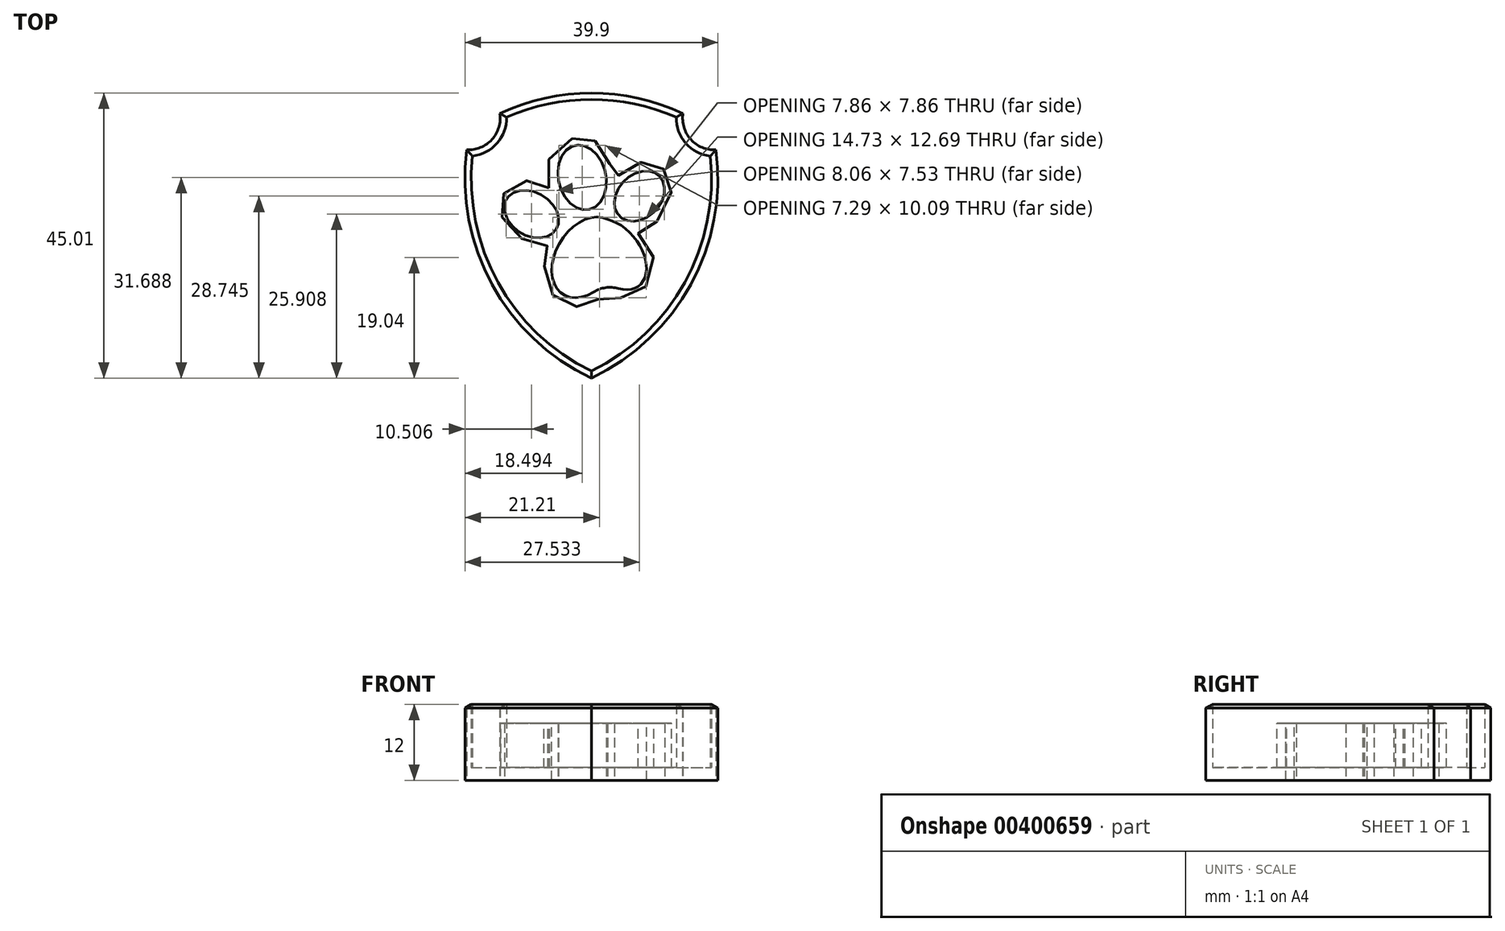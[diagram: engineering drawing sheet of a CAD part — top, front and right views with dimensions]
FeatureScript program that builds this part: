
annotation { "Feature Type Name" : "Feature", "Feature Type Description" : "" }
export const myFeature = defineFeature(function(context is Context, id is Id, definition is map)
    precondition{}
    {
        {
            var Q0;
            Q0=qCreatedBy(makeId("Top.planeOp"),FACE);
            var sketch = newSketch(context, id + "F0", { "sketchPlane" : qUnion([Q0])});
            skLineSegment(sketch, "E0", {"start": v(0, 25) * mm, "end": v(0, -25) * mm, "construction": true});
            skArc(sketch, "E1", {"start": v(-14.44, 19.95) * mm, "mid": v(0, 23.16) * mm, "end": v(14.44, 19.95) * mm});
            skArc(sketch, "E2", {"start": v(-14.44, 19.95) * mm, "mid": v(-15.68, 15.84) * mm, "end": v(-19.65, 14.2) * mm});
            skArc(sketch, "E3", {"start": v(14.44, 19.95) * mm, "mid": v(15.68, 15.84) * mm, "end": v(19.65, 14.2) * mm});
            skArc(sketch, "E4", {"start": v(0, -21.85) * mm, "mid": v(-15.7, -7.03) * mm, "end": v(-19.65, 14.2) * mm});
            skArc(sketch, "E5", {"start": v(19.65, 14.2) * mm, "mid": v(15.7, -7.03) * mm, "end": v(0, -21.85) * mm});
            skSolve(sketch);
        }
        {
            var Q0;
            Q0=qSketchRegion(id+"F0",true);
            extrude(context, id + "F1", {"entities" : qUnion([Q0]), "depth" : 2 * mm});
        }
        {
            var Q0;
            Q0=qCreatedBy(makeId("Top.planeOp"),FACE);
            var sketch = newSketch(context, id + "F2", { "sketchPlane" : qUnion([Q0])});
            skArc(sketch, "E6.0", {"start": v(-14.44, 19.95) * mm, "mid": v(0, 23.16) * mm, "end": v(14.44, 19.95) * mm});
            skArc(sketch, "E6.1", {"start": v(-14.44, 19.95) * mm, "mid": v(-15.68, 15.84) * mm, "end": v(-19.65, 14.2) * mm});
            skArc(sketch, "E6.2", {"start": v(0, -21.85) * mm, "mid": v(-15.7, -7.03) * mm, "end": v(-19.65, 14.2) * mm});
            skArc(sketch, "E6.3", {"start": v(14.44, 19.95) * mm, "mid": v(15.68, 15.84) * mm, "end": v(19.65, 14.2) * mm});
            skArc(sketch, "E7.0", {"start": v(-13.39, 19.33) * mm, "mid": v(-14.89, 15.23) * mm, "end": v(-18.76, 13.22) * mm});
            skArc(sketch, "E7.1", {"start": v(0, -20.74) * mm, "mid": v(-14.73, -6.71) * mm, "end": v(-18.76, 13.22) * mm});
            skArc(sketch, "E7.2", {"start": v(-13.39, 19.33) * mm, "mid": v(0, 22.16) * mm, "end": v(13.39, 19.33) * mm});
            skArc(sketch, "E7.3", {"start": v(13.39, 19.33) * mm, "mid": v(14.89, 15.23) * mm, "end": v(18.76, 13.22) * mm});
            skArc(sketch, "E7.4", {"start": v(18.76, 13.22) * mm, "mid": v(14.73, -6.71) * mm, "end": v(0, -20.74) * mm});
            skArc(sketch, "E8.0", {"start": v(19.65, 14.2) * mm, "mid": v(15.7, -7.03) * mm, "end": v(0, -21.85) * mm});
            skSolve(sketch);
        }
        {
            var Q0;
            Q0=qSketchRegion(id+"F2",true);
            extrude(context, id + "F3", {"entities" : qUnion([Q0]), "operationType" : NewBodyOperationType.ADD, "depth" : 12 * mm});
        }
        {
            var Q0;
            Q0=qCreatedBy(makeId("Top.planeOp"),FACE);
            var sketch = newSketch(context, id + "F4", { "sketchPlane" : qUnion([Q0])});
            skEllipse(sketch, "E9", {"center": v(-9.44, 4.06) * mm, "majorRadius": 4.58 * mm, "minorRadius": 3.42 * mm, "majorAxis": v(0.85, -0.53)});
            skEllipse(sketch, "E10", {"center": v(-1.46, 9.84) * mm, "majorRadius": 5.18 * mm, "minorRadius": 3.74 * mm, "majorAxis": v(0.22, -0.97)});
            skEllipse(sketch, "E11", {"center": v(7.58, 6.9) * mm, "majorRadius": 4.46 * mm, "minorRadius": 3.4 * mm, "majorAxis": v(0.7, 0.7)});
            skEllipticalArc(sketch, "E12", {});
            skEllipticalArc(sketch, "E13", {});
            skPoint(sketch, "E14.visualSharp", {"position": v(2.19, -6.69) * mm});
            skArc(sketch, "E14.filletArc", {"start": v(4.29, -7.69) * mm, "mid": v(2.25, -7.56) * mm, "end": v(0.34, -8.26) * mm});
            const initialGuessF4  = {"E12": [-0.000825658324174583, -0.0027743864338845015, 0.5189781024771581, 0.8547875345073818, 0.006885848797741289, 0.004767301582334577, 0.046636328894096385, 4.077954499657045], "E13": [0.0034836893901228905, -0.0022488562390208244, 0.6385724586285335, -0.7695617032318526, 0.006419216435122319, 0.004185572444733501, 5.533444123706438, 2.4160858860053582]};
            skSetInitialGuess(sketch, initialGuessF4);
            skSolve(sketch);
        }
        {
            var Q0;
            Q0=qCreatedBy(makeId("Top.planeOp"),FACE);
            var sketch = newSketch(context, id + "F5", { "sketchPlane" : qUnion([Q0])});
            skFitSpline(sketch, "E15", {"points": [v(-6.71, 8.16) * mm, v(-9.02, 9.2) * mm, v(-13.12, 8.16) * mm, v(-14.28, 5.63) * mm, v(-13.33, 2.06) * mm, v(-9.02, -0.57) * mm, v(-6.71, -1.2) * mm, v(-7.34, -3.83) * mm, v(-6.3, -8.45) * mm, v(-2.82, -10.55) * mm, v(-0.09, -9.92) * mm, v(2.43, -9.08) * mm, v(5.7, -9.08) * mm, v(9.26, -6.35) * mm, v(9.26, -1.4) * mm, v(7.37, 1.32) * mm, v(10.32, 2.9) * mm, v(12.63, 7.95) * mm, v(11.58, 11) * mm, v(8.84, 12.15) * mm, v(5.59, 11.52) * mm, v(3.48, 9.63) * mm, v(2.43, 13.73) * mm, v(0.02, 15.83) * mm, v(-2.82, 16.04) * mm, v(-6.71, 12.57) * mm, v(-6.71, 8.16) * mm]});
            skSolve(sketch);
        }
        {
            var Q0;
            Q0=qSketchRegion(id+"F5",true);
            extrude(context, id + "F6", {"entities" : qUnion([Q0]), "operationType" : NewBodyOperationType.ADD, "depth" : 9 * mm});
        }
        {
            var Q0;
            Q0=qSketchRegion(id+"F4",true);
            extrude(context, id + "F7", {"entities" : qUnion([Q0]), "operationType" : NewBodyOperationType.REMOVE, "endBound" : BoundingType.THROUGH_ALL, "depth" : 25 * mm});
        }
        {
            var Q0;
            Q0=makeQuery(id+"F3.opExtrude","CAP_EDGE",EDGE,{"disambiguationData":[OSD([sQuery(id+"F2.wireOp",EDGE,"E6.2")])],"isStart":false});
            var Q1;
            Q1=makeQuery(id+"F3.opExtrude","CAP_EDGE",EDGE,{"disambiguationData":[OSD([sQuery(id+"F2.wireOp",EDGE,"E6.1")])],"isStart":false});
            var Q2;
            Q2=makeQuery(id+"F3.opExtrude","CAP_EDGE",EDGE,{"disambiguationData":[OSD([sQuery(id+"F2.wireOp",EDGE,"E6.0")])],"isStart":false});
            var Q3;
            Q3=makeQuery(id+"F3.opExtrude","CAP_EDGE",EDGE,{"disambiguationData":[OSD([sQuery(id+"F2.wireOp",EDGE,"E6.3")])],"isStart":false});
            var Q4;
            Q4=makeQuery(id+"F3.opExtrude","CAP_EDGE",EDGE,{"disambiguationData":[OSD([sQuery(id+"F2.wireOp",EDGE,"E8.0")])],"isStart":false});
            chamfer(context, id + "F8", {"entities" : qUnion([Q0, Q1, Q2, Q3, Q4]), "chamferType" : ChamferType.OFFSET_ANGLE, "width" : 1 * mm, "oppositeDirection" : false, "angle" : 30 * degree, "tangentPropagation" : true});
        }
    });
